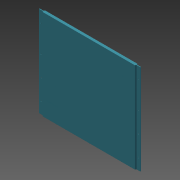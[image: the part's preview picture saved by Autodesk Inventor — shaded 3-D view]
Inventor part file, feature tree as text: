
AUTODESK INVENTOR PART (.ipt)
format: ipt  version: 2015 (Build 190159000, 159)  size: 314,368 bytes
history: native  units: mm
features: sketch x4, extrude x3, fillet x3, other x1, shell x1, hole x1
ambient origin geometry x8: Origin, YZ Plane, XZ Plane, XY Plane, X Axis, Y Axis, Z Axis, Center Point
bodies: Body1 (feature_tree)
feature tree (13):
  other  "Bryła1"
  extrude  "Wyciągnięcie proste1"  Depth=17.5mm
  shell  "Skorupa1"  Thickness=1.0mm
  fillet  "Zaokrąglenie1"  Radius=1.0mm
  fillet  "Zaokrąglenie3"  Radius=3.0mm
  extrude  "Wyciągnięcie proste3"  Depth=17.5mm
  extrude  "Wyciągnięcie proste4"  Depth=448.5mm
  fillet  "Zaokrąglenie4"  Radius=11.5mm
  hole  "Otwór2"  [1 undecoded]
  sketch  "Szkic1"
  sketch  "Szkic3"
  sketch  "Szkic4"
  sketch  "Szkic5"
note: 1 required parameter value undecoded (feature->parameter linkage not recoverable at this tier; creation-order binding heuristic only, values carry confidence <= 0.55)
